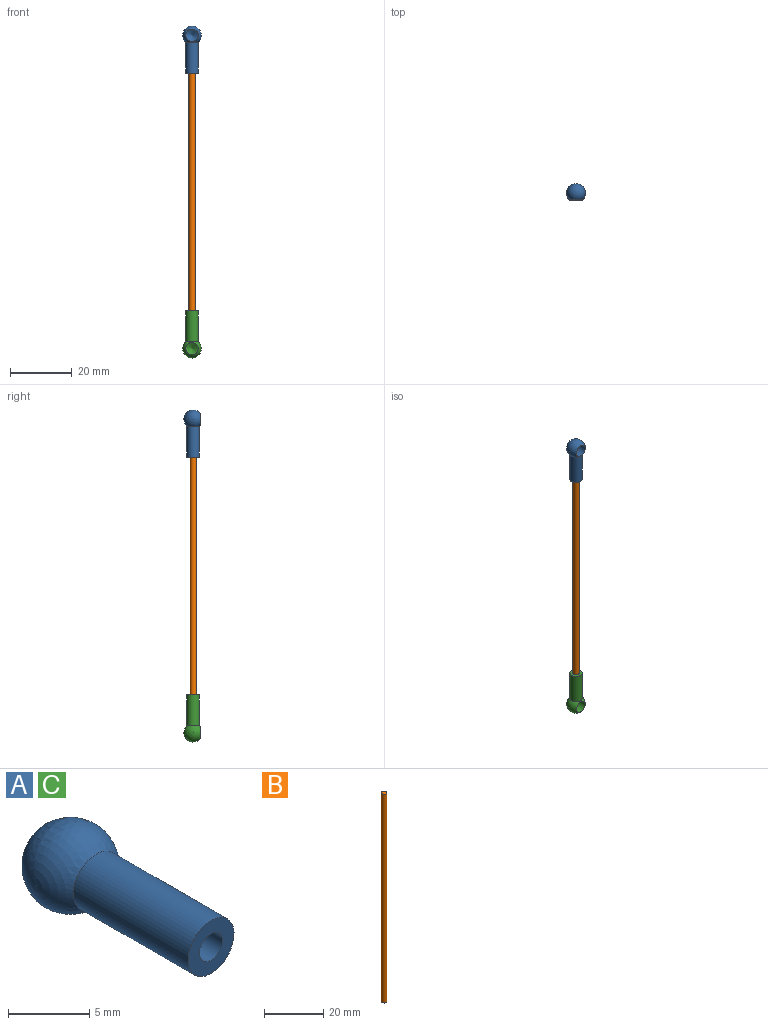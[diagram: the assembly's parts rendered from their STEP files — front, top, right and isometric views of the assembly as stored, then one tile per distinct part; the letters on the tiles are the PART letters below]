
ASSEMBLY  parts=3 mates=2
PART A: 7 faces, bbox 6x15.2x6 mm
  f0: cylinder r=2mm len=10mm, axis (0,1,0), area 125.9mm2, adj f1,f2
  f1: plane 4.01x4.01mm, normal (0,-1,0), area 9.5mm2, adj f0,f4
  f2: sphere r=3mm, area 84.2mm2, adj f0,f6
  f3: cone r=1mm half-angle=59deg, axis (0,-1,0), area 3.7mm2, adj f4
  f4: cylinder r=1mm len=8mm, axis (0,-1,0), area 50.3mm2, adj f1,f3
  f5: cone r=2mm half-angle=59deg, axis (0,0,-1), area 14.7mm2, adj f6
  f6: cylinder r=2mm len=4mm, axis (0,0,-1), area 40.7mm2, adj f2,f5
PART B: 3 faces, bbox 2x2x86 mm
  f0: cylinder r=1mm len=86mm, axis (0,0,-1), area 540.4mm2, adj f1,f2
  f1: plane 2x2mm, normal (0,0,1), area 3.1mm2, adj f0
  f2: plane 2x2mm, normal (0,0,-1), area 3.1mm2, adj f0
PART C: same geometry as A
PLACE A rot(axis=(0,0.71,0.71),180deg) t=(0,0,94.03)mm
PLACE B at identity fixed
PLACE C rot(axis=(-1,0,0),90deg) t=(0,0,-7.23)mm
MATE fastened C.f0 <-> B.f0  axis (0,0,1) through (0,0,5)mm
MATE fastened A.f0 <-> B.f0  axis (0,0,-1) through (0,0,81.8)mm
